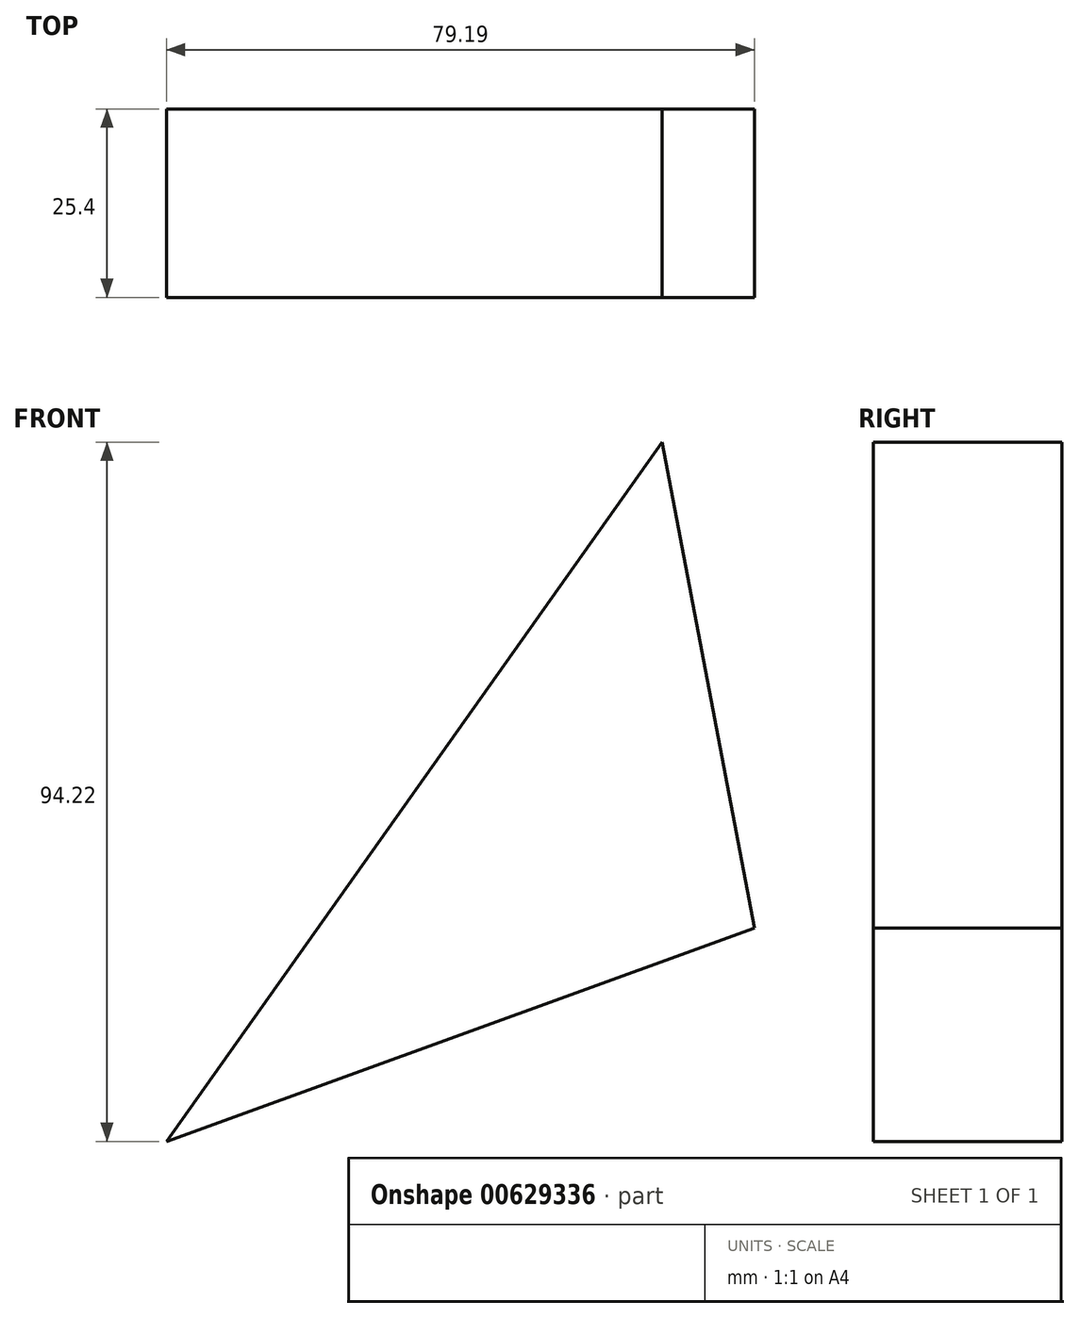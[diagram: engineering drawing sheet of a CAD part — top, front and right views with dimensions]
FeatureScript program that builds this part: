
annotation { "Feature Type Name" : "Feature", "Feature Type Description" : "" }
export const myFeature = defineFeature(function(context is Context, id is Id, definition is map)
    precondition{}
    {
        {
            var Q0;
            Q0=qCreatedBy(makeId("Front.planeOp"),FACE);
            var sketch = newSketch(context, id + "F0", { "sketchPlane" : qUnion([Q0])});
            skLineSegment(sketch, "E0", {"start": v(0, 0) * mm, "end": v(66.72, 94.22) * mm});
            skLineSegment(sketch, "E1", {"start": v(66.72, 94.22) * mm, "end": v(79.19, 28.74) * mm});
            skLineSegment(sketch, "E2", {"start": v(79.19, 28.74) * mm, "end": v(0, 0) * mm});
            skSolve(sketch);
        }
        {
            var Q0;
            Q0=makeQuery(id+"F0.imprint","IMPRINT",FACE,{"disambiguationData":[TD([[makeQuery(id+"F0.imprint","IMPRINT",EDGE,{"derivedFrom":sQuery(id+"F0.wireOp",EDGE,"E0")}),-1.0]])]});
            extrude(context, id + "F1", {"entities" : qUnion([Q0]), "depth" : 25.4 * mm, "offsetDistance" : 25.4 * mm});
        }
    });
